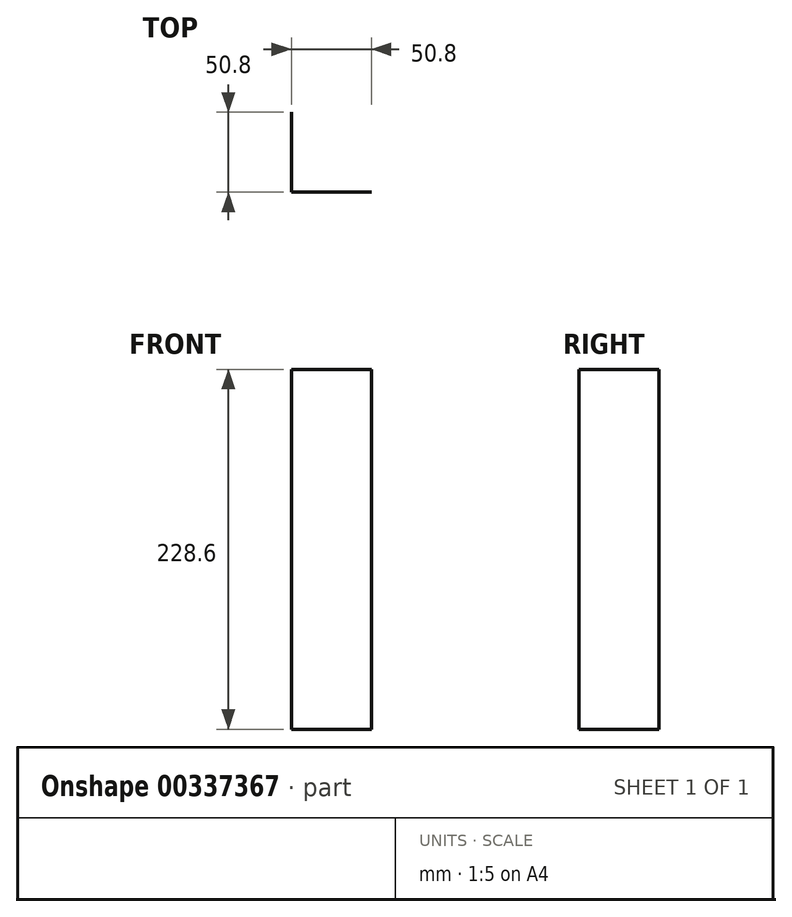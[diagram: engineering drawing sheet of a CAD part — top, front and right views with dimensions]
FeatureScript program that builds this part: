
annotation { "Feature Type Name" : "Feature", "Feature Type Description" : "" }
export const myFeature = defineFeature(function(context is Context, id is Id, definition is map)
    precondition{}
    {
        {
            var Q0;
            Q0=qCreatedBy(makeId("Top.planeOp"),FACE);
            var sketch = newSketch(context, id + "F0", { "sketchPlane" : qUnion([Q0])});
            skLineSegment(sketch, "E0", {"start": v(-54.11, 20.44) * mm, "end": v(-54.11, -30.36) * mm});
            skLineSegment(sketch, "E1", {"start": v(-54.11, -30.36) * mm, "end": v(-3.31, -30.36) * mm});
            skSolve(sketch);
        }
        {
            var Q0;
            Q0 = qSketchRegion(id + "F0", true);
            var Q1;
            Q1=sQuery(id+"F0.wireOp",EDGE,"E0");
            var Q2;
            Q2=sQuery(id+"F0.wireOp",EDGE,"E1");
            extrude(context, id + "F1", {"entities" : qUnion([Q0]), "bodyType" : ToolBodyType.SURFACE, "surfaceEntities" : qUnion([Q1, Q2]), "depth" : 228.6 * mm});
        }
    });
